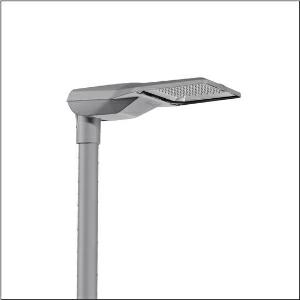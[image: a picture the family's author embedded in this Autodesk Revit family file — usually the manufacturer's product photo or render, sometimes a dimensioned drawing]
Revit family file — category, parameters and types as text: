
# Revit family: streetlight_sl_21_midi___stw1_0a_5xe7e33a08nb_8300
name_source: partatom
category: Lighting Fixtures
units: mm (PartAtom-declared; Revit-internal decimal feet)

## family parameters
Cut with Voids When Loaded = No
Host = Face
Light Source = No
Part Type = Normal
Room Calculation Point = No
Round Connector Dimension = Use Diameter
Shared = No

## types (1)
- --- (1 x LED, 22700 lm, 151.2 W, 3000K)
    Apparent Load = 151 VA
    CIE Flux Codes = 39 75 98 100 100
    Color Rendering = 70
    Color Temperature = 3000K
    Default Elevation = 1800 mm
    Description = Streetlight SL 21 midi, mast luminaire, primary light control with lens, of PMMA, primary optical cover: cover, of toughened safety glass, transparent, light distribution: STW1.0a, light emission: direct distribution, primary light characteristic: asymmetric, installation type: post-top, side-entry, LED, 3G 1.5mm², High Power LED, rated luminous flux: 22.700lm, luminous efficacy: 150lm/W, light colour: 730, colour temperature: 3000K, control: overheat protection, constant luminous flux control, time-dependent luminous flux control, flexible luminous flux parameterisation, mains connection: 220..240V, AC, 50/60Hz, connection cable pre-assembled, cable length: 12,5m, wiring characteristics: H07RN-F, start of lifetime: 151W, end of service life: 157W, reduction: 70W, luminaire housing, of diecast aluminium, powder-coated, Siteco® metallic grey (DB 702S), corrosivity category C5 mid according to DIN EN ISO 12944, please order mast flange separately, inclination adjustable: 0°, 5°, 10°, 15°, sealing non-destructively replaceable, multi-level sealing system, length: 644mm, width: 335mm, height: 110mm, mast flange for spigot size: 42mm (side-entry): 5XC10008XM4, 60/48mm (side-entry/post-top): 5XC10108XM2, 76/60mm (side-entry/post-top): 5XC10108XM1, protection rating (complete): IP66, insulation class (complete): insulation class II (safety insulation), certification: CE, ENEC, ENEC+, VDE, impact resistance: IK09, permissible operating ambient temperature for outdoor applications: -40..+50°C, standard-compliant lighting for roads and squares, packaging unit: 1 piece

Light Distribution: STW1.0a
    Height = 111 mm
    Lamp = 1 x LED
    Lamp Light Flux = 22700 lm
    Lamp Power = 151.2 W
    Lamp count = 1
    Length = 644 mm
    Luminous efficacy = 150 lm/W
    Manufacturer = Siteco
    ModVariant = No
    Model = 5XE7E33A08NB
    Number of Poles = 1
    OnlyDefault = Yes
    Power Factor = 1
    Product Name = Streetlight SL 21 midi | STW1.0a
    Product group = mast luminaire | pylon top
    ProductGroupID = 6100
    Protection Class = Protection class II
    Protection Degree = IP 66
    RLX_Detail_Level = 1
    RLX_Emergency_Light_Flux = 0 lm
    RLX_Emergency_Type = 0
    RLX_Emergency_Type_DB = No
    RlxData = <blob elided: 90953 chars, md5=65c94720>
    Socket = socket
    Standby Power = 0 W
    System Light Flux = 22700 lm
    System Power = 151 W
    Type Comments = factory setting: luminous flux: 100 % | Output Level: 100 % | 802 mA
    Type Image = l_1004298.jpg
    URL = http://relux.com
    VarID = @adj_119853
    Voltage = 0 V
    Weight = 0.00 kg
    Width = 336 mm

## geometry (parser evidence)
native form markers: Blend x4, Sweep x10
no freeform markers — native parametric forms only
